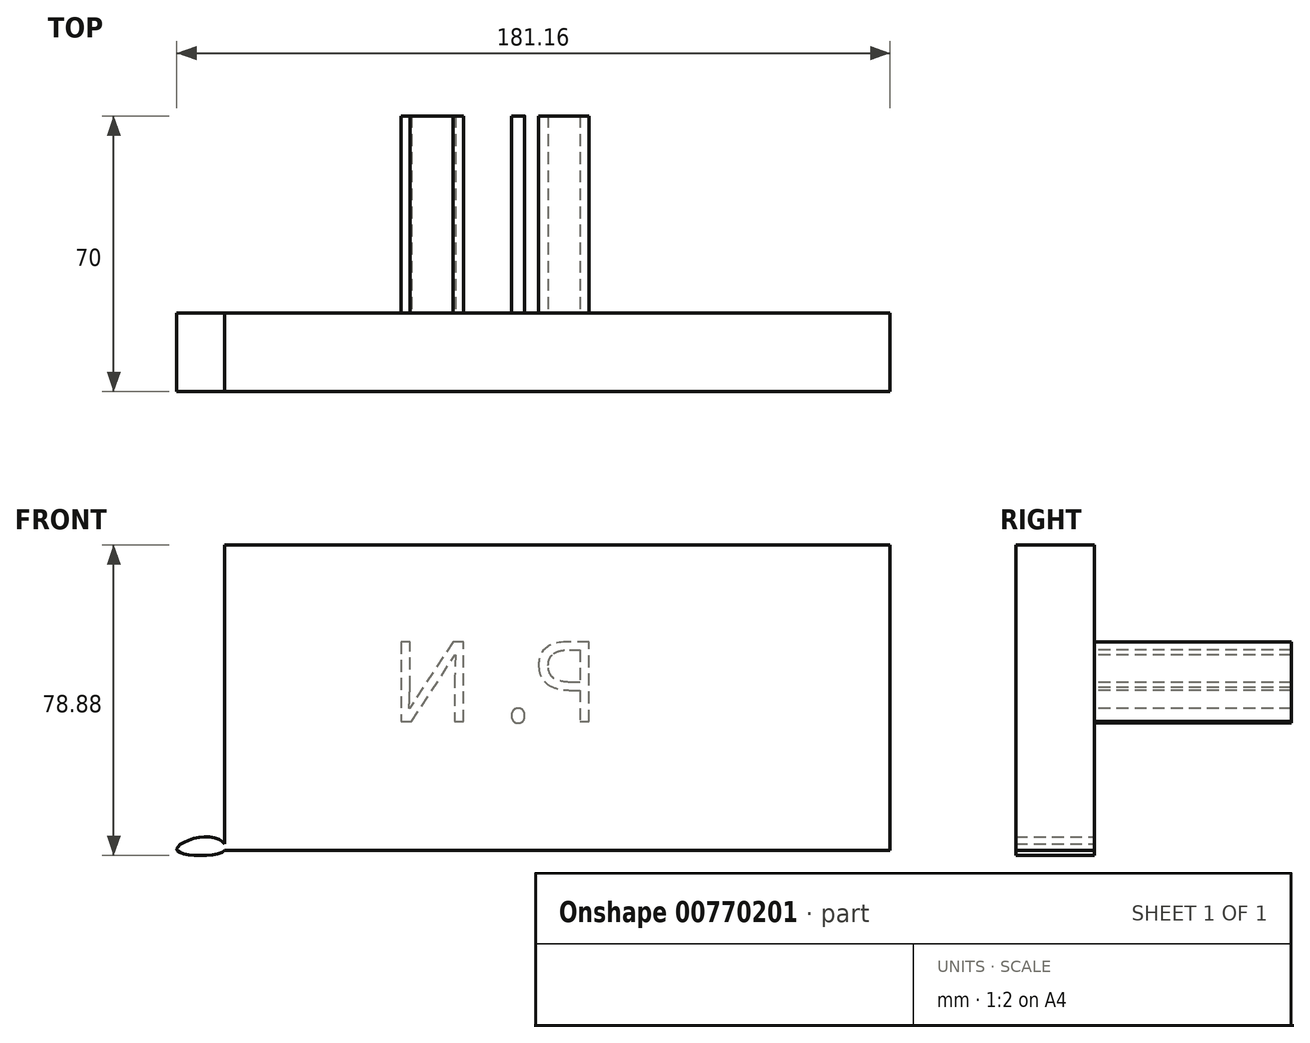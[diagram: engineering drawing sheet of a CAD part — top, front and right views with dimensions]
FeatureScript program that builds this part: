
annotation { "Feature Type Name" : "Feature", "Feature Type Description" : "" }
export const myFeature = defineFeature(function(context is Context, id is Id, definition is map)
    precondition{}
    {
        {
            var Q0;
            Q0=qCreatedBy(makeId("Front.planeOp"),FACE);
            var sketch = newSketch(context, id + "F0", { "sketchPlane" : qUnion([Q0])});
            skLineSegment(sketch, "E0.bottom", {"start": v(-42.97, 41.82) * mm, "end": v(126.03, 41.82) * mm});
            skLineSegment(sketch, "E0.top", {"start": v(-42.97, -35.78) * mm, "end": v(126.03, -35.78) * mm});
            skLineSegment(sketch, "E0.left", {"start": v(-42.97, 41.82) * mm, "end": v(-42.97, -35.78) * mm});
            skLineSegment(sketch, "E0.right", {"start": v(126.03, 41.82) * mm, "end": v(126.03, -35.78) * mm});
            skFitSpline(sketch, "E1", {"points": [v(-42.97, -35.78) * mm, v(-46.7, -32.33) * mm, v(-55.04, -35.78) * mm, v(-42.97, -35.78) * mm]});
            skPoint(sketch, "E2.2.internal.orphan", {"position": v(-55.04, 41.82) * mm});
            skSolve(sketch);
        }
        {
            var Q0;
            Q0 = qSketchRegion(id + "F0", true);
            extrude(context, id + "F1", {"entities" : qUnion([Q0]), "depth" : 20 * mm, "offsetDistance" : 25 * mm});
        }
        {
            var Q0;
            Q0=makeQuery(id+"F1.opExtrude","CAP_FACE",FACE,{"disambiguationData":[OSD([sQuery(id+"F0.wireOp",EDGE,"E0.bottom"),sQuery(id+"F0.wireOp",EDGE,"E0.top"),sQuery(id+"F0.wireOp",EDGE,"E0.left"),sQuery(id+"F0.wireOp",EDGE,"E0.right"),sQuery(id+"F0.wireOp",EDGE,"E1")])],"isStart":true});
            var sketch = newSketch(context, id + "F2", { "sketchPlane" : qUnion([Q0])});
            skText(sketch, "E3", { "text": "P. N", "fontName": "OpenSans-Regular.ttf"});
            const initialGuessF2  = {"E3": [-0.0524, -0.00302, 1, 0, 0.0204]};
            skSetInitialGuess(sketch, initialGuessF2);
            skSolve(sketch);
        }
        {
            var Q0;
            Q0 = qSketchRegion(id + "F2", true);
            extrude(context, id + "F3", {"entities" : qUnion([Q0]), "operationType" : NewBodyOperationType.ADD, "depth" : 50 * mm, "offsetDistance" : 25 * mm});
        }
    });
